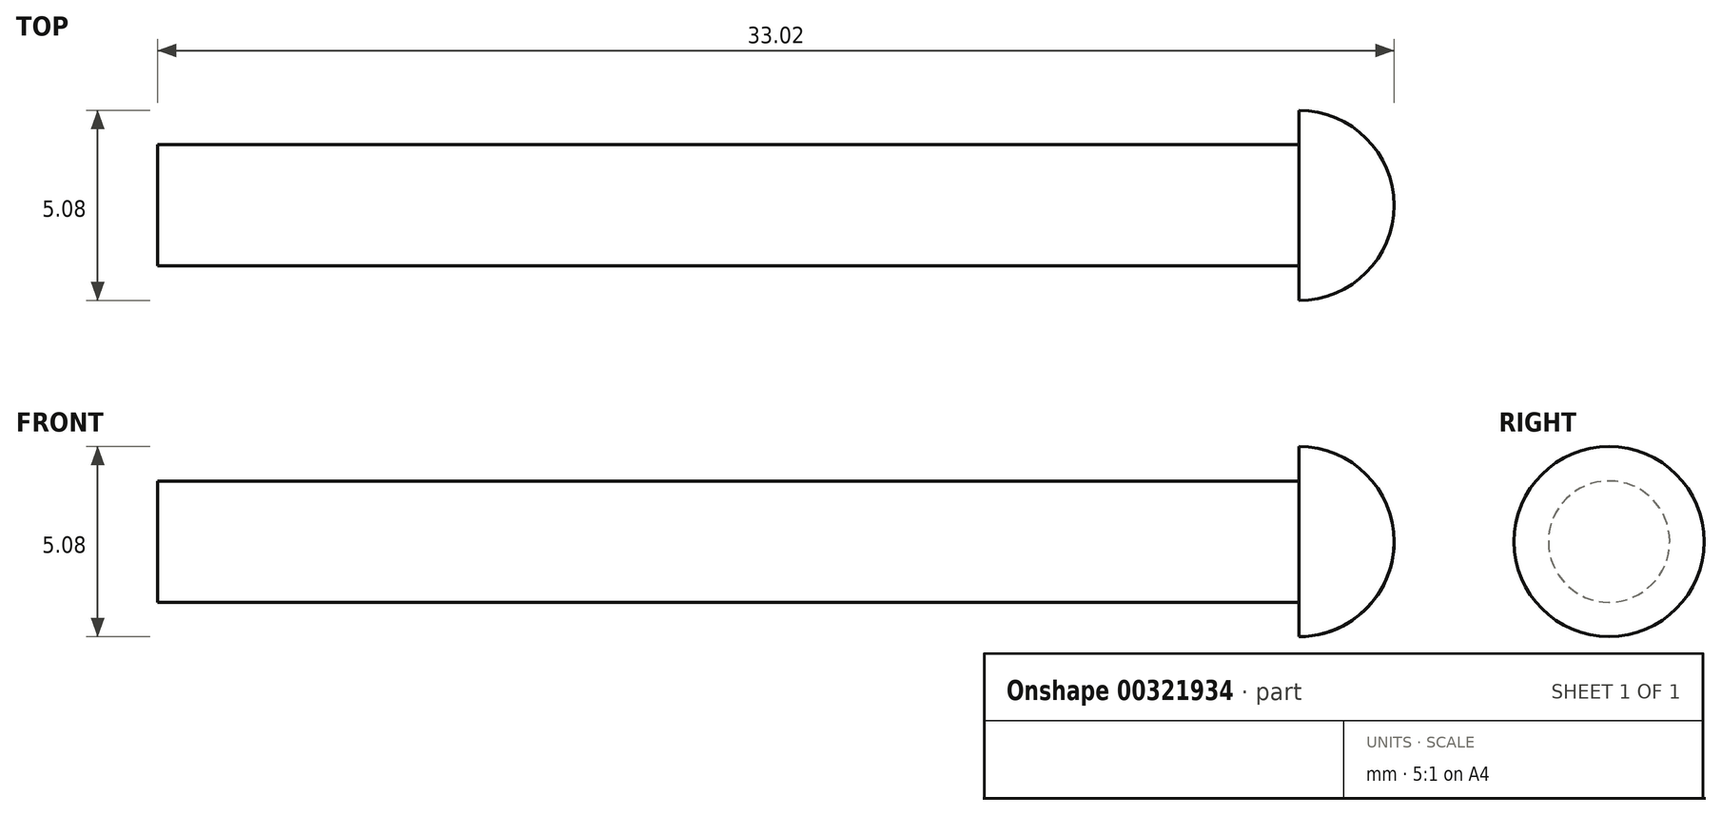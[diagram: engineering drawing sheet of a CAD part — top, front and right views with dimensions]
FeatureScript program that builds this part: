
annotation { "Feature Type Name" : "Feature", "Feature Type Description" : "" }
export const myFeature = defineFeature(function(context is Context, id is Id, definition is map)
    precondition{}
    {
        {
            var Q0;
            Q0=qCreatedBy(makeId("Front.planeOp"),FACE);
            var sketch = newSketch(context, id + "F0", { "sketchPlane" : qUnion([Q0])});
            skLineSegment(sketch, "E0", {"start": v(0, 0) * mm, "end": v(30.48, 0) * mm});
            skArc(sketch, "E1", {"start": v(33.02, 0) * mm, "mid": v(32.28, 1.8) * mm, "end": v(30.48, 2.54) * mm});
            skLineSegment(sketch, "E2", {"start": v(30.48, 0) * mm, "end": v(33.02, 0) * mm});
            skLineSegment(sketch, "E3", {"start": v(30.48, 1.62) * mm, "end": v(30.48, 2.54) * mm});
            skLineSegment(sketch, "E4", {"start": v(0, 0) * mm, "end": v(0, 1.62) * mm});
            skLineSegment(sketch, "E5", {"start": v(0, 1.62) * mm, "end": v(30.48, 1.62) * mm});
            skLineSegment(sketch, "E6", {"start": v(-6.23, 0) * mm, "end": v(38.1, 0) * mm, "construction": true});
            skSolve(sketch);
        }
        {
            var Q0;
            Q0 = qSketchRegion(id + "F0", true);
            var Q1;
            Q1=sQuery(id+"F0.wireOp",EDGE,"E6");
            revolve(context, id + "F1", {"entities" : qUnion([Q0]), "axis" : qUnion([Q1]), "revolveType" : RevolveType.FULL});
        }
    });
